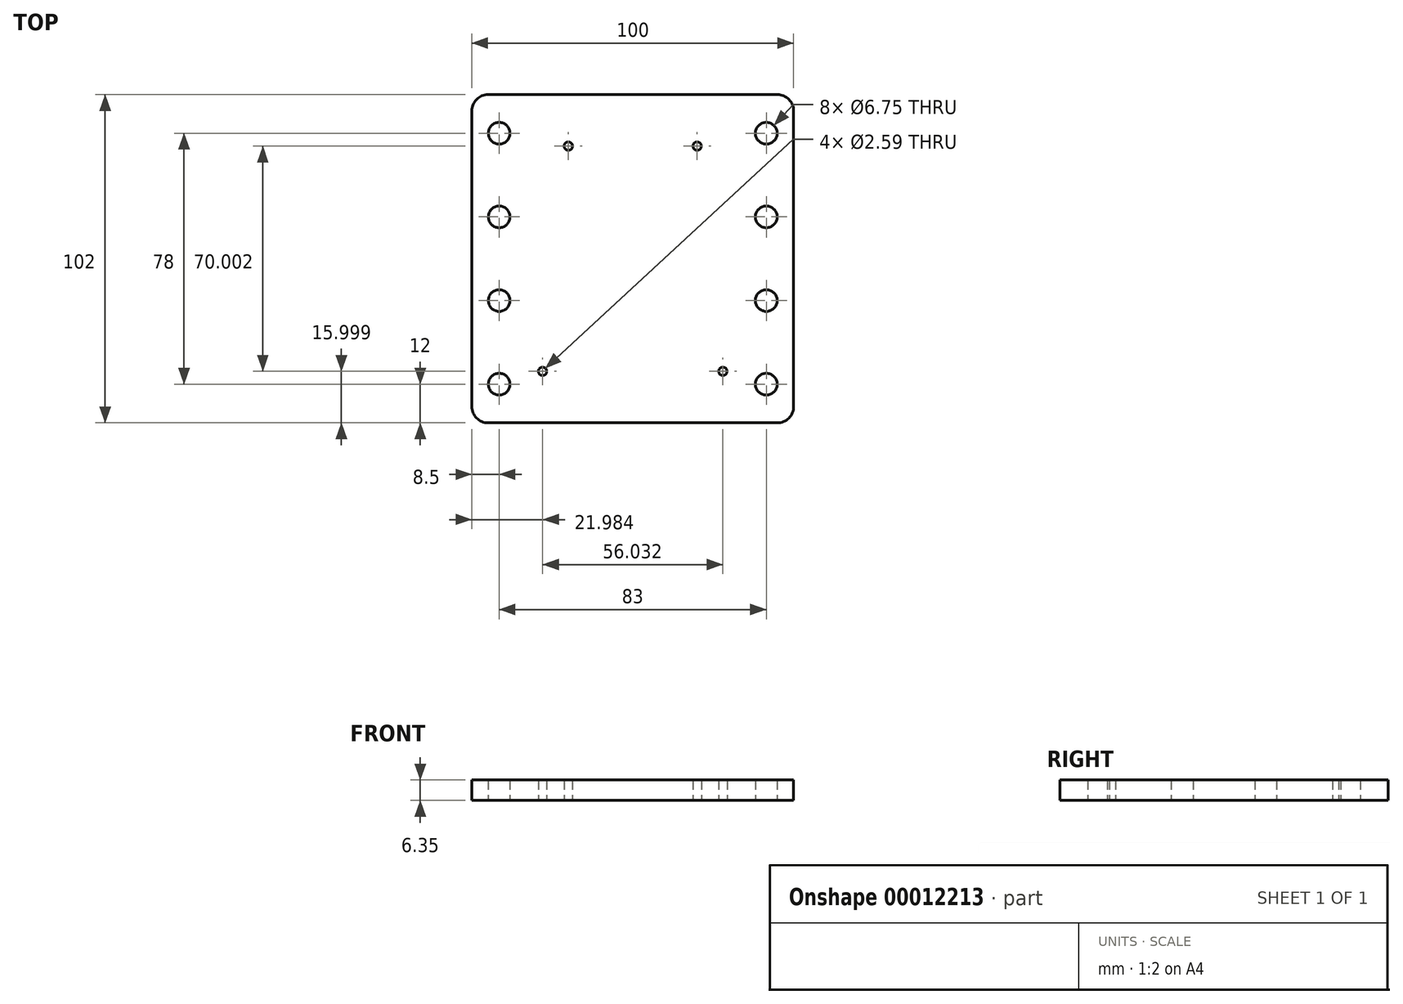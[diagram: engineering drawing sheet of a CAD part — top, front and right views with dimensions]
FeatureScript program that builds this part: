
annotation { "Feature Type Name" : "Feature", "Feature Type Description" : "" }
export const myFeature = defineFeature(function(context is Context, id is Id, definition is map)
    precondition{}
    {
        {
            var Q0;
            Q0=qCreatedBy(makeId("Top.planeOp"),FACE);
            var sketch = newSketch(context, id + "F0", { "sketchPlane" : qUnion([Q0])});
            skCircle(sketch, "E0", {"center": v(-20.02, 35) * mm, "radius": 1.3 * mm});
            skCircle(sketch, "E1", {"center": v(-28.02, -35) * mm, "radius": 1.3 * mm});
            skCircle(sketch, "E2.0.MirrorC", {"center": v(20.02, 35) * mm, "radius": 1.3 * mm});
            skCircle(sketch, "E3.0.MirrorC", {"center": v(28.02, -35) * mm, "radius": 1.3 * mm});
            skCircle(sketch, "E4", {"center": v(-41.5, 39) * mm, "radius": 3.38 * mm});
            skCircle(sketch, "E5", {"center": v(-41.5, 13) * mm, "radius": 3.38 * mm});
            skCircle(sketch, "E6", {"center": v(-41.5, -13) * mm, "radius": 3.38 * mm});
            skCircle(sketch, "E7", {"center": v(-41.5, -39) * mm, "radius": 3.38 * mm});
            skLineSegment(sketch, "E8", {"start": v(-41.5, 39) * mm, "end": v(-41.5, -39) * mm, "construction": true});
            skCircle(sketch, "E9.0.MirrorC", {"center": v(41.5, 39) * mm, "radius": 3.38 * mm});
            skCircle(sketch, "E10.0.MirrorC", {"center": v(41.5, 13) * mm, "radius": 3.38 * mm});
            skCircle(sketch, "E11.0.MirrorC", {"center": v(41.5, -13) * mm, "radius": 3.38 * mm});
            skCircle(sketch, "E12.0.MirrorC", {"center": v(41.5, -39) * mm, "radius": 3.38 * mm});
            skLineSegment(sketch, "E13.rect.bottom", {"start": v(44.92, 51) * mm, "end": v(-44.92, 51) * mm});
            skLineSegment(sketch, "E13.rect.top", {"start": v(44.92, -51) * mm, "end": v(-44.92, -51) * mm});
            skLineSegment(sketch, "E13.rect.left", {"start": v(50, 45.92) * mm, "end": v(50, -45.92) * mm});
            skLineSegment(sketch, "E13.rect.right", {"start": v(-50, 45.92) * mm, "end": v(-50, -45.92) * mm});
            skPoint(sketch, "E13.rect.middle", {"position": v(0, 0) * mm});
            skPoint(sketch, "E14.visualSharp", {"position": v(-50, 51) * mm});
            skArc(sketch, "E14.filletArc", {"start": v(-44.92, 51) * mm, "mid": v(-48.51, 49.51) * mm, "end": v(-50, 45.92) * mm});
            skPoint(sketch, "E15.visualSharp", {"position": v(50, 51) * mm});
            skArc(sketch, "E15.filletArc", {"start": v(50, 45.92) * mm, "mid": v(48.51, 49.51) * mm, "end": v(44.92, 51) * mm});
            skPoint(sketch, "E16.visualSharp", {"position": v(50, -51) * mm});
            skArc(sketch, "E16.filletArc", {"start": v(44.92, -51) * mm, "mid": v(48.51, -49.51) * mm, "end": v(50, -45.92) * mm});
            skPoint(sketch, "E17.visualSharp", {"position": v(-50, -51) * mm});
            skArc(sketch, "E17.filletArc", {"start": v(-50, -45.92) * mm, "mid": v(-48.51, -49.51) * mm, "end": v(-44.92, -51) * mm});
            skSolve(sketch);
        }
        {
            var Q0;
            Q0 = qSketchRegion(id + "F0", true);
            extrude(context, id + "F1", {"entities" : qUnion([Q0]), "depth" : 6.35 * mm});
        }
    });
